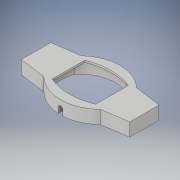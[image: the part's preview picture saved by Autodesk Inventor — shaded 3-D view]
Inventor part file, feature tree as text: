
AUTODESK INVENTOR PART (.ipt)
format: ipt  version: 2019 (Build 230136000, 136)  size: 1,505,792 bytes
history: native  units: mm
features: sketch x8, extrude x5, other x5, projected_geometry x5, revolve x2, plane x1, fillet x1
ambient origin geometry x8: Origin, YZ Plane, XZ Plane, XY Plane, X Axis, Y Axis, Z Axis, Center Point
bodies: Volumenkörper1 (feature_tree)
feature tree (27):
  sketch  "Skizze1"  dims[d9=15.2mm d12=13.036764mm]
  sketch  "Skizze2"  dims[d38=15.2mm d47=8.714705mm]
  sketch  "Skizze3"  dims[d49=8.715mm d57=15.197209mm]
  extrude  "Extrusion1"  Depth=13.036764mm
  extrude  "Extrusion3"  Depth=8.714705mm
  extrude  "Extrusion4"  Depth=15.197209mm
  extrude  "Extrusion5"  Depth=11.912488mm
  plane  "Arbeitsebene3"
  other  "Trennen3"
  fillet  "Rundung5"  Radius=1.077mm
  extrude  "Extrusion6"  Depth=3.1mm
  revolve  "Umdrehung2"
  revolve  "Umdrehung3"
  other  "Bild2"
  other  "Bild3"
  other  "Bild4"
  sketch  "Skizze8"  dims[d58=15.197209mm d59=11.912488mm d60=1.077mm]
  projected_geometry  "Projizierte Kontur4"
  sketch  "Skizze9"  dims[d61=3.1mm d62=0.0mm d67=8.853mm]
  projected_geometry  "Projizierte Kontur5"
  sketch  "Skizze10"  dims[d69=0.0mm]
  projected_geometry  "Projizierte Kontur6"
  projected_geometry  "Projizierte Kontur7"
  sketch  "Skizze12"  dims[d70=8.853mm]
  projected_geometry  "Projizierte Kontur8"
  sketch  "Skizze13"  dims[d73=0.5mm d74=0.0mm d75=0.6mm d76=90.0deg d77=1.55mm d78=0.5mm d79=0.0mm d80=5.0mm d81=5.0mm d82=8.798192mm d83=8.798192mm d84=4.0mm d85=4.0mm d86=4.8mm d87=0.0mm d91=1.745329mm d92=1.0mm d95=2.3mm d96=0.0mm d98=-2.268928mm d102=1.0mm d103=1.745329mm d104=1.0mm d105=1.0mm]
  other  "Arbeitsachse4"
